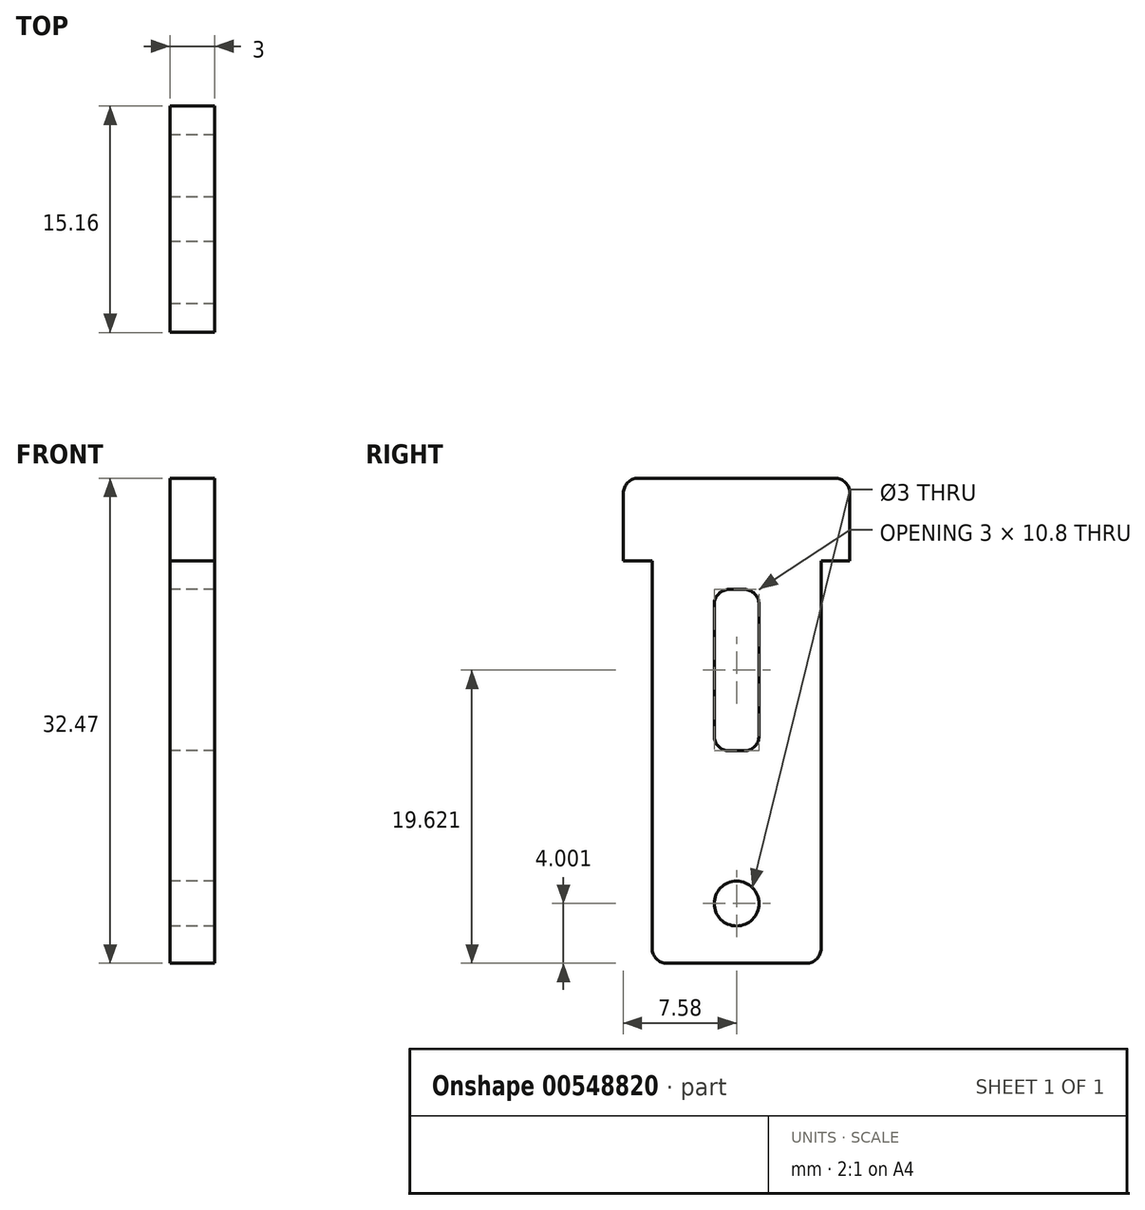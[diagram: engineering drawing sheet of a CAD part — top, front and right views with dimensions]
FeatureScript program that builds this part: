
annotation { "Feature Type Name" : "Feature", "Feature Type Description" : "" }
export const myFeature = defineFeature(function(context is Context, id is Id, definition is map)
    precondition{}
    {
        {
            var Q0;
            Q0=qCreatedBy(makeId("Right.planeOp"),FACE);
            var sketch = newSketch(context, id + "F0", { "sketchPlane" : qUnion([Q0])});
            skLineSegment(sketch, "E0.bottom", {"start": v(-6.58, 6.06) * mm, "end": v(6.57, 6.06) * mm});
            skLineSegment(sketch, "E0.top", {"start": v(-4.65, -26.4) * mm, "end": v(4.65, -26.4) * mm});
            skLineSegment(sketch, "E0.left", {"start": v(-7.58, 5.06) * mm, "end": v(-7.58, 0.51) * mm});
            skLineSegment(sketch, "E0.right", {"start": v(7.57, 5.06) * mm, "end": v(7.57, 0.51) * mm});
            skLineSegment(sketch, "E1", {"start": v(6.58, 0.51) * mm, "end": v(-6.58, 0.51) * mm, "construction": true});
            skLineSegment(sketch, "E2", {"start": v(5.65, 16) * mm, "end": v(5.65, -25.4) * mm, "construction": true});
            skLineSegment(sketch, "E3", {"start": v(5.65, -33.33) * mm, "end": v(-5.65, -33.33) * mm, "construction": true});
            skLineSegment(sketch, "E4", {"start": v(-5.65, -25.4) * mm, "end": v(-5.65, 17.41) * mm, "construction": true});
            skLineSegment(sketch, "E5", {"start": v(-7.58, 0.51) * mm, "end": v(-5.65, 0.51) * mm});
            skLineSegment(sketch, "E6", {"start": v(-5.65, 0.51) * mm, "end": v(-5.65, -26.4) * mm});
            skLineSegment(sketch, "E7", {"start": v(5.65, -26.4) * mm, "end": v(5.65, 0.51) * mm});
            skLineSegment(sketch, "E8", {"start": v(5.65, 0.51) * mm, "end": v(7.58, 0.51) * mm});
            skLineSegment(sketch, "E9", {"start": v(-0.5, -1.39) * mm, "end": v(0.5, -1.39) * mm, "construction": true});
            skLineSegment(sketch, "E10.bottom", {"start": v(-1.5, -1.39) * mm, "end": v(1.5, -1.39) * mm});
            skLineSegment(sketch, "E10.top", {"start": v(-0.5, -12.19) * mm, "end": v(0.5, -12.19) * mm});
            skLineSegment(sketch, "E10.left", {"start": v(-1.5, -2.39) * mm, "end": v(-1.5, -11.19) * mm});
            skLineSegment(sketch, "E10.right", {"start": v(1.5, -2.39) * mm, "end": v(1.5, -11.19) * mm});
            skPoint(sketch, "E11.visualSharp", {"position": v(-7.58, 6.06) * mm});
            skArc(sketch, "E11.filletArc", {"start": v(-6.58, 6.06) * mm, "mid": v(-7.28, 5.77) * mm, "end": v(-7.58, 5.06) * mm});
            skPoint(sketch, "E12.visualSharp", {"position": v(7.58, 6.06) * mm});
            skArc(sketch, "E12.filletArc", {"start": v(7.57, 5.06) * mm, "mid": v(7.28, 5.77) * mm, "end": v(6.57, 6.06) * mm});
            skPoint(sketch, "E13.newPointA", {"position": v(15.85, -1.39) * mm});
            skArc(sketch, "E13.filletArc", {"start": v(1.5, -2.39) * mm, "mid": v(1.2, -1.68) * mm, "end": v(0.5, -1.39) * mm});
            skPoint(sketch, "E14.newPointB", {"position": v(-18.85, -1.39) * mm});
            skArc(sketch, "E14.filletArc", {"start": v(-0.5, -1.39) * mm, "mid": v(-1.2, -1.68) * mm, "end": v(-1.5, -2.39) * mm});
            skPoint(sketch, "E15.visualSharp", {"position": v(-1.5, -12.19) * mm});
            skArc(sketch, "E15.filletArc", {"start": v(-1.5, -11.19) * mm, "mid": v(-1.2, -11.9) * mm, "end": v(-0.5, -12.19) * mm});
            skPoint(sketch, "E16.visualSharp", {"position": v(1.5, -12.19) * mm});
            skArc(sketch, "E16.filletArc", {"start": v(0.5, -12.19) * mm, "mid": v(1.2, -11.9) * mm, "end": v(1.5, -11.19) * mm});
            skLineSegment(sketch, "E17", {"start": v(-13.1, -25.57) * mm, "end": v(10.75, -25.57) * mm, "construction": true});
            skLineSegment(sketch, "E18", {"start": v(10.75, -25.57) * mm, "end": v(10.75, -24.07) * mm, "construction": true});
            skLineSegment(sketch, "E19", {"start": v(10.75, -24.07) * mm, "end": v(-14.98, -24.07) * mm, "construction": true});
            skArc(sketch, "E20.filletArc", {"start": v(-5.65, -25.4) * mm, "mid": v(-5.36, -26.12) * mm, "end": v(-4.65, -26.4) * mm});
            skArc(sketch, "E21.filletArc", {"start": v(4.65, -26.4) * mm, "mid": v(5.36, -26.12) * mm, "end": v(5.65, -25.4) * mm});
            skPoint(sketch, "E22", {"position": v(0, -25.57) * mm});
            skCircle(sketch, "E23", {"center": v(0, -22.4) * mm, "radius": 1.5 * mm});
            skSolve(sketch);
        }
        {
            var Q0;
            Q0=makeQuery(id+"F0.imprint","IMPRINT",FACE,{"disambiguationData":[TD([[makeQuery(id+"F0.imprint","IMPRINT",EDGE,{"derivedFrom":sQuery(id+"F0.wireOp",EDGE,"E0.bottom")}),-1.0]])]});
            extrude(context, id + "F1", {"entities" : qUnion([Q0]), "depth" : 3 * mm, "offsetDistance" : 25 * mm});
        }
    });
